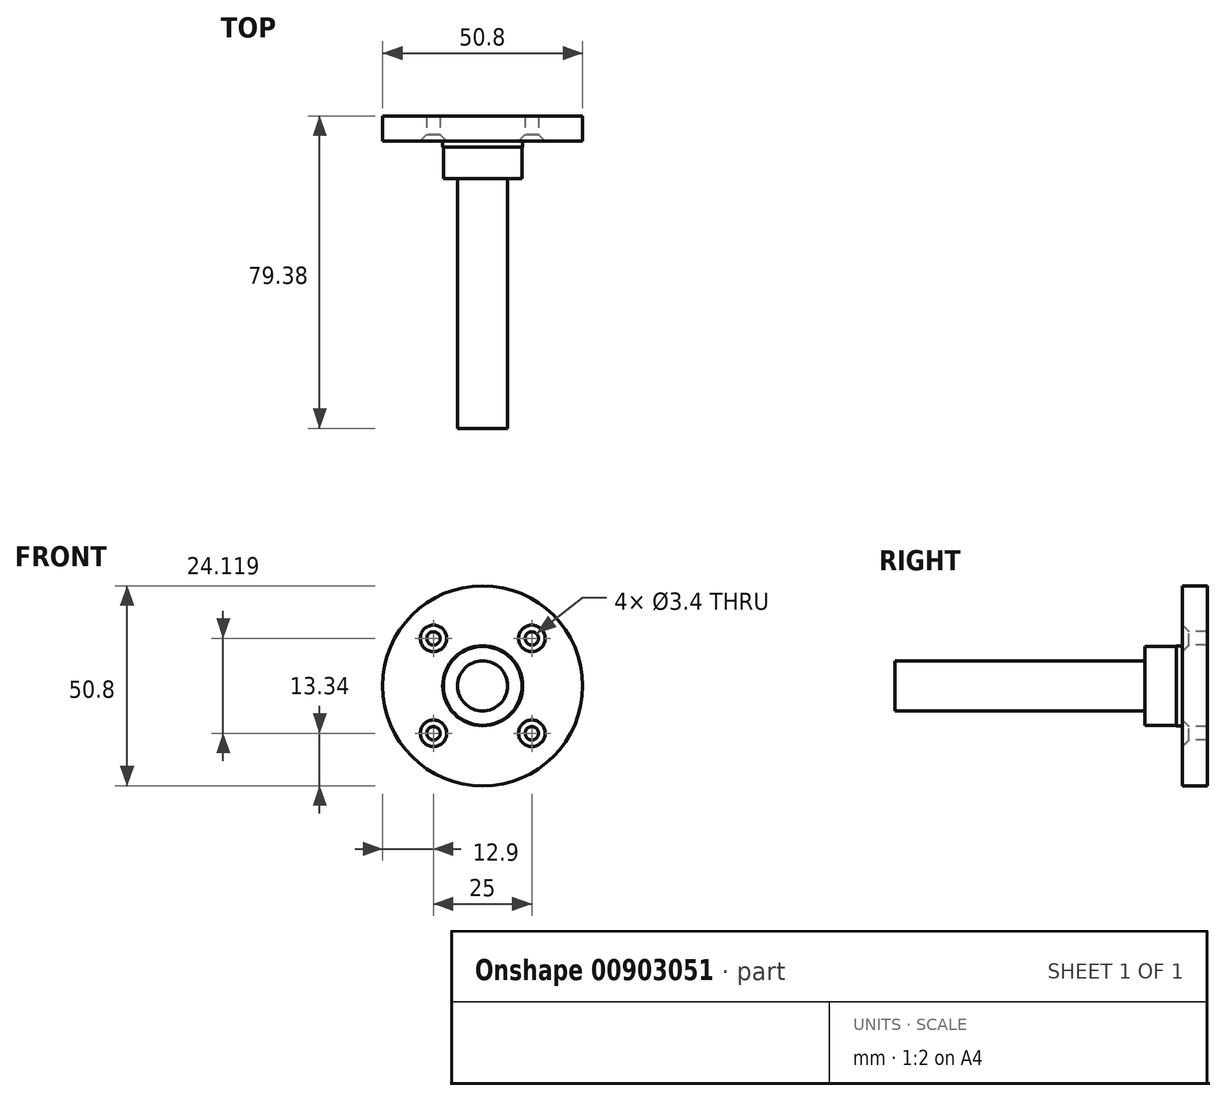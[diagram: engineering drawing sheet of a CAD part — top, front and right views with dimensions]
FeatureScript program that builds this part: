
annotation { "Feature Type Name" : "Feature", "Feature Type Description" : "" }
export const myFeature = defineFeature(function(context is Context, id is Id, definition is map)
    precondition{}
    {
        {
            var Q0;
            Q0=qCreatedBy(makeId("Front.planeOp"),FACE);
            var sketch = newSketch(context, id + "F0", { "sketchPlane" : qUnion([Q0])});
            skLineSegment(sketch, "E0.bottom", {"start": v(-12.5, 12.5) * mm, "end": v(12.5, 12.5) * mm, "construction": true});
            skLineSegment(sketch, "E0.top", {"start": v(-12.5, -12.5) * mm, "end": v(12.5, -12.5) * mm, "construction": true});
            skLineSegment(sketch, "E0.left", {"start": v(-12.5, 12.5) * mm, "end": v(-12.5, -12.5) * mm, "construction": true});
            skLineSegment(sketch, "E0.right", {"start": v(12.5, 12.5) * mm, "end": v(12.5, -12.5) * mm, "construction": true});
            skPoint(sketch, "E0.middle", {"position": v(0, 0) * mm});
            skCircle(sketch, "E1", {"center": v(0, 0) * mm, "radius": 25.4 * mm});
            skSolve(sketch);
        }
        {
            var Q0;
            Q0 = qSketchRegion(id + "F0", true);
            extrude(context, id + "F1", {"entities" : qUnion([Q0]), "depth" : 6.35 * mm, "offsetDistance" : 25.4 * mm});
        }
        {
            var Q0;
            Q0=makeQuery(id+"F1.opExtrude","CAP_FACE",FACE,{"disambiguationData":[OSD([sQuery(id+"F0.wireOp",EDGE,"E1")])],"isStart":false});
            var sketch = newSketch(context, id + "F2", { "sketchPlane" : qUnion([Q0])});
            skLineSegment(sketch, "E2.bottom", {"start": v(12.5, 12.06) * mm, "end": v(-12.5, 12.06) * mm});
            skLineSegment(sketch, "E2.top", {"start": v(12.5, -12.06) * mm, "end": v(-12.5, -12.06) * mm});
            skLineSegment(sketch, "E2.left", {"start": v(12.5, 12.06) * mm, "end": v(12.5, -12.06) * mm});
            skLineSegment(sketch, "E2.right", {"start": v(-12.5, 12.06) * mm, "end": v(-12.5, -12.06) * mm});
            skPoint(sketch, "E2.middle", {"position": v(0, 0) * mm});
            skSolve(sketch);
        }
        {
            var Q0;
            Q0=sQuery(id+"F2.wireOp",VERTEX,"E2.bottom.end");
            var Q1;
            Q1=sQuery(id+"F2.wireOp",VERTEX,"E2.bottom.start");
            var Q2;
            Q2=sQuery(id+"F2.wireOp",VERTEX,"E2.top.start");
            var Q3;
            Q3=sQuery(id+"F2.wireOp",VERTEX,"E2.top.end");
            var Q4;
            Q4=makeQuery(id+"F1.opExtrude","SWEPT_BODY",BODY,{"disambiguationData":[OSD([sQuery(id+"F0.wireOp",EDGE,"E1")])]});
            hole(context, id + "F3", {"style" : HoleStyle.C_SINK, "endStyle" : HoleEndStyle.THROUGH, "standardTappedOrClearance" : lookupTablePath({ "fit" : "Normal", "standard" : "ISO", "size" : "M3", "type" : "Clearance" }), "standardBlindInLast" : lookupTablePath({ "fit" : "Normal", "standard" : "ISO", "engagement" : "75%", "pitch" : "0.5 mm", "size" : "M3", "type" : "Clearance & tapped" }), "holeDiameter" : 3.4 * mm, "cSinkDiameter" : 6.72 * mm, "cSinkAngle" : 90 * degree, "majorDiameter" : 6.35 * mm, "isTappedThrough" : true, "tappedDepth" : 12.7 * mm, "tapClearance" : 3, "locations" : qUnion([Q0, Q1, Q2, Q3]), "scope" : qUnion([Q4])});
        }
        {
            var Q0;
            Q0=makeQuery(id+"F1.opExtrude","CAP_FACE",FACE,{"disambiguationData":[OSD([sQuery(id+"F0.wireOp",EDGE,"E1")])],"isStart":false});
            var sketch = newSketch(context, id + "F4", { "sketchPlane" : qUnion([Q0])});
            skCircle(sketch, "E3", {"center": v(0, 0) * mm, "radius": 10.16 * mm});
            skSolve(sketch);
        }
        {
            var Q0;
            Q0=makeQuery(id+"F4.imprint","IMPRINT",FACE,{"disambiguationData":[TD([[makeQuery(id+"F4.imprint","IMPRINT",EDGE,{"derivedFrom":sQuery(id+"F4.wireOp",EDGE,"E3")}),1.0]])]});
            extrude(context, id + "F5", {"entities" : qUnion([Q0]), "operationType" : NewBodyOperationType.ADD, "depth" : 9.52 * mm, "offsetDistance" : 25.4 * mm});
        }
        {
            var Q0;
            Q0=makeQuery(id+"F5.opExtrude","CAP_FACE",FACE,{"disambiguationData":[OSD([sQuery(id+"F4.wireOp",EDGE,"E3")])],"isStart":false});
            var sketch = newSketch(context, id + "F6", { "sketchPlane" : qUnion([Q0])});
            skCircle(sketch, "E4", {"center": v(0, 0) * mm, "radius": 10 * mm});
            skSolve(sketch);
        }
        {
            var Q0;
            Q0=makeQuery(id+"F6.imprint","IMPRINT",FACE,{"disambiguationData":[TD([[makeQuery(id+"F6.imprint","IMPRINT",EDGE,{"derivedFrom":sQuery(id+"F6.wireOp",EDGE,"E4")}),-1.0]])]});
            extrude(context, id + "F7", {"entities" : qUnion([Q0]), "operationType" : NewBodyOperationType.REMOVE, "oppositeDirection" : true, "depth" : 8 * mm, "offsetDistance" : 25.4 * mm});
        }
        {
            var Q0;
            Q0=makeQuery(id+"F5.opExtrude","CAP_FACE",FACE,{"disambiguationData":[OSD([sQuery(id+"F4.wireOp",EDGE,"E3")])],"isStart":false});
            var sketch = newSketch(context, id + "F8", { "sketchPlane" : qUnion([Q0])});
            skCircle(sketch, "E5", {"center": v(0, 0) * mm, "radius": 6.35 * mm});
            skSolve(sketch);
        }
        {
            var Q0;
            Q0 = qSketchRegion(id + "F8", true);
            extrude(context, id + "F9", {"entities" : qUnion([Q0]), "operationType" : NewBodyOperationType.ADD, "depth" : 63.5 * mm, "offsetDistance" : 25.4 * mm});
        }
    });
